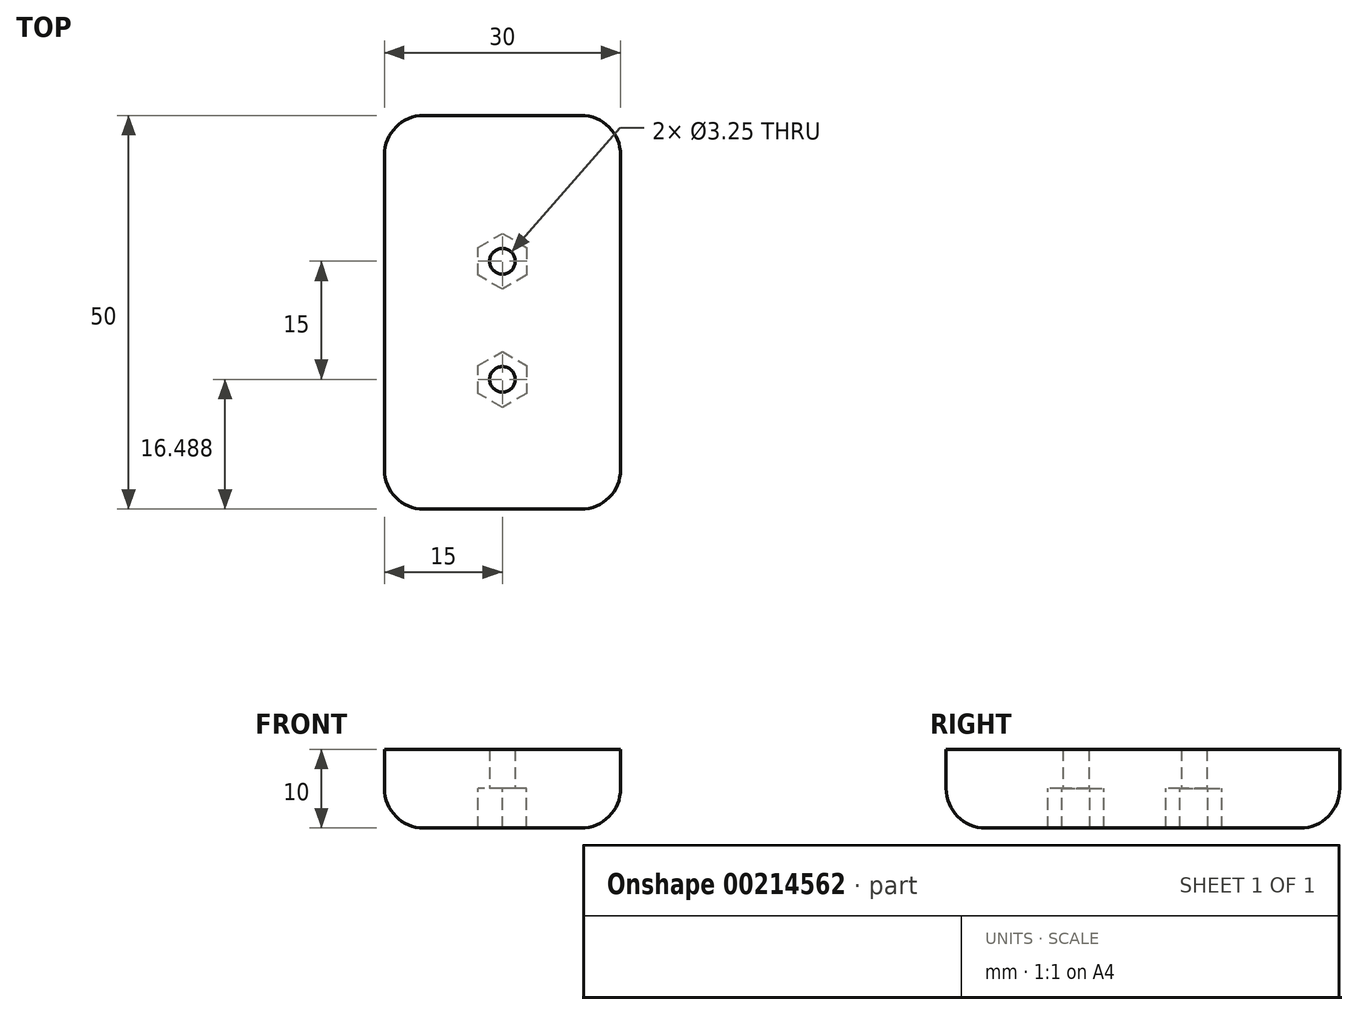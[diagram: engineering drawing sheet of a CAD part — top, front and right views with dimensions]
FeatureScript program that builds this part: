
annotation { "Feature Type Name" : "Feature", "Feature Type Description" : "" }
export const myFeature = defineFeature(function(context is Context, id is Id, definition is map)
    precondition{}
    {
        {
            var Q0;
            Q0=qCreatedBy(makeId("Top.planeOp"),FACE);
            var sketch = newSketch(context, id + "F0", { "sketchPlane" : qUnion([Q0])});
            skCircle(sketch, "E0.cCircle", {"center": v(0, 31.49) * mm, "radius": 3.55 * mm, "construction": true});
            skLineSegment(sketch, "E0.0", {"start": v(0, 27.94) * mm, "end": v(-3.07, 29.71) * mm});
            skLineSegment(sketch, "E0.1", {"start": v(-3.07, 29.71) * mm, "end": v(-3.07, 33.26) * mm});
            skLineSegment(sketch, "E0.2", {"start": v(-3.07, 33.26) * mm, "end": v(0, 35.04) * mm});
            skLineSegment(sketch, "E0.3", {"start": v(0, 35.04) * mm, "end": v(3.07, 33.26) * mm});
            skLineSegment(sketch, "E0.4", {"start": v(3.07, 33.26) * mm, "end": v(3.07, 29.71) * mm});
            skLineSegment(sketch, "E0.5", {"start": v(3.07, 29.71) * mm, "end": v(0, 27.94) * mm});
            skCircle(sketch, "E1.cCircle", {"center": v(0, 16.49) * mm, "radius": 3.55 * mm, "construction": true});
            skLineSegment(sketch, "E1.0", {"start": v(3.07, 14.71) * mm, "end": v(0, 12.94) * mm});
            skLineSegment(sketch, "E1.1", {"start": v(0, 12.94) * mm, "end": v(-3.07, 14.71) * mm});
            skLineSegment(sketch, "E1.2", {"start": v(-3.07, 14.71) * mm, "end": v(-3.07, 18.26) * mm});
            skLineSegment(sketch, "E1.3", {"start": v(-3.07, 18.26) * mm, "end": v(0, 20.04) * mm});
            skLineSegment(sketch, "E1.4", {"start": v(0, 20.04) * mm, "end": v(3.07, 18.26) * mm});
            skLineSegment(sketch, "E1.5", {"start": v(3.07, 18.26) * mm, "end": v(3.07, 14.71) * mm});
            skLineSegment(sketch, "E2.left", {"start": v(-15, 0) * mm, "end": v(-15, 50) * mm});
            skLineSegment(sketch, "E2.right", {"start": v(15, 0) * mm, "end": v(15, 50) * mm});
            skLineSegment(sketch, "E3", {"start": v(15, 50) * mm, "end": v(0, 50) * mm});
            skLineSegment(sketch, "E4", {"start": v(0, 50) * mm, "end": v(-15, 50) * mm});
            skLineSegment(sketch, "E5", {"start": v(-15, 0) * mm, "end": v(0, 0) * mm});
            skLineSegment(sketch, "E6", {"start": v(0, 0) * mm, "end": v(15, 0) * mm});
            skSolve(sketch);
        }
        {
            var Q0;
            Q0=makeQuery(id+"F0.imprint","IMPRINT",FACE,{"disambiguationData":[TD([[makeQuery(id+"F0.imprint","IMPRINT",EDGE,{"derivedFrom":sQuery(id+"F0.wireOp",EDGE,"E0.0")}),1.0]])]});
            extrude(context, id + "F1", {"entities" : qUnion([Q0]), "oppositeDirection" : true, "depth" : 5 * mm});
        }
        {
            var Q0;
            Q0=qCreatedBy(makeId("Top.planeOp"),FACE);
            var sketch = newSketch(context, id + "F2", { "sketchPlane" : qUnion([Q0])});
            skLineSegment(sketch, "E7.bottom", {"start": v(-15, 50) * mm, "end": v(15, 50) * mm});
            skLineSegment(sketch, "E7.top", {"start": v(-15, 0) * mm, "end": v(15, 0) * mm});
            skLineSegment(sketch, "E7.left", {"start": v(-15, 50) * mm, "end": v(-15, 0) * mm});
            skLineSegment(sketch, "E7.right", {"start": v(15, 50) * mm, "end": v(15, 0) * mm});
            skSolve(sketch);
        }
        {
            var Q0;
            Q0 = qSketchRegion(id + "F2", true);
            extrude(context, id + "F3", {"entities" : qUnion([Q0]), "operationType" : NewBodyOperationType.ADD, "depth" : 5 * mm});
        }
        {
            var Q0;
            Q0=makeQuery(id+"F1.opExtrude","CAP_FACE",FACE,{"disambiguationData":[OSD([sQuery(id+"F0.wireOp",EDGE,"E0.0"),sQuery(id+"F0.wireOp",EDGE,"E0.1"),sQuery(id+"F0.wireOp",EDGE,"E0.2"),sQuery(id+"F0.wireOp",EDGE,"E0.3"),sQuery(id+"F0.wireOp",EDGE,"E0.4"),sQuery(id+"F0.wireOp",EDGE,"E0.5"),sQuery(id+"F0.wireOp",EDGE,"E1.0"),sQuery(id+"F0.wireOp",EDGE,"E1.1"),sQuery(id+"F0.wireOp",EDGE,"E1.2"),sQuery(id+"F0.wireOp",EDGE,"E1.3"),sQuery(id+"F0.wireOp",EDGE,"E1.4"),sQuery(id+"F0.wireOp",EDGE,"E1.5"),sQuery(id+"F0.wireOp",EDGE,"E2.left"),sQuery(id+"F0.wireOp",EDGE,"E2.right"),sQuery(id+"F0.wireOp",EDGE,"E3"),sQuery(id+"F0.wireOp",EDGE,"E4"),sQuery(id+"F0.wireOp",EDGE,"E5"),sQuery(id+"F0.wireOp",EDGE,"E6")])],"isStart":false});
            var sketch = newSketch(context, id + "F4", { "sketchPlane" : qUnion([Q0])});
            skCircle(sketch, "E8", {"center": v(0, -16.49) * mm, "radius": 1.62 * mm});
            skPoint(sketch, "E8.centerSnap0", {"position": v(-3.07, -16.49) * mm});
            skPoint(sketch, "E8.perimeterSnap0", {"position": v(-3.07, -16.49) * mm});
            skPoint(sketch, "E8.perimeterSnap1", {"position": v(1.54, -19.15) * mm});
            skCircle(sketch, "E9", {"center": v(0, -31.49) * mm, "radius": 1.62 * mm});
            skPoint(sketch, "E9.centerSnap0", {"position": v(3.07, -31.49) * mm});
            skPoint(sketch, "E9.perimeterSnap0", {"position": v(3.07, -31.49) * mm});
            skSolve(sketch);
        }
        {
            var Q0;
            Q0=makeQuery(id+"F4.imprint","IMPRINT",FACE,{"disambiguationData":[TD([[makeQuery(id+"F4.imprint","IMPRINT",EDGE,{"derivedFrom":sQuery(id+"F4.wireOp",EDGE,"E8")}),1.0]])]});
            var Q1;
            Q1=makeQuery(id+"F4.imprint","IMPRINT",FACE,{"disambiguationData":[TD([[makeQuery(id+"F4.imprint","IMPRINT",EDGE,{"derivedFrom":sQuery(id+"F4.wireOp",EDGE,"E9")}),1.0]])]});
            var Q2;
            Q2=sQuery(id+"F4.wireOp",EDGE,"E9");
            var Q3;
            Q3=sQuery(id+"F4.wireOp",EDGE,"E8");
            extrude(context, id + "F5", {"entities" : qUnion([Q0, Q1]), "operationType" : NewBodyOperationType.REMOVE, "surfaceEntities" : qUnion([Q2, Q3]), "oppositeDirection" : true, "depth" : 25 * mm});
        }
        {
            var Q0;
            Q0=makeQuery(id+"F1.opExtrude","CAP_EDGE",EDGE,{"disambiguationData":[OSD([sQuery(id+"F0.wireOp",EDGE,"E5"),sQuery(id+"F0.wireOp",EDGE,"E6")])],"isStart":false});
            var Q1;
            Q1=makeQuery(id+"F1.opExtrude","CAP_EDGE",EDGE,{"disambiguationData":[OSD([sQuery(id+"F0.wireOp",EDGE,"E2.left")])],"isStart":false});
            var Q2;
            Q2=makeQuery(id+"F1.opExtrude","CAP_EDGE",EDGE,{"disambiguationData":[OSD([sQuery(id+"F0.wireOp",EDGE,"E2.right")])],"isStart":false});
            var Q3;
            Q3=makeQuery(id+"F1.opExtrude","CAP_EDGE",EDGE,{"disambiguationData":[OSD([sQuery(id+"F0.wireOp",EDGE,"E3"),sQuery(id+"F0.wireOp",EDGE,"E4")])],"isStart":false});
            var Q4;
            Q4=makeQuery(id+"F3.boolean.opBoolean","MERGE",EDGE,{"derivedFrom":[makeQuery(id+"F1.opExtrude","SWEPT_EDGE",EDGE,{"disambiguationData":[OSD([sQuery(id+"F0.wireOp",EDGE,"E2.right"),sQuery(id+"F0.wireOp",EDGE,"E3")])]}),makeQuery(id+"F3.opExtrude","SWEPT_EDGE",EDGE,{"disambiguationData":[OSD([sQuery(id+"F2.wireOp",EDGE,"E7.bottom"),sQuery(id+"F2.wireOp",EDGE,"E7.right")])]})]});
            var Q5;
            Q5=makeQuery(id+"F3.boolean.opBoolean","MERGE",EDGE,{"derivedFrom":[makeQuery(id+"F1.opExtrude","SWEPT_EDGE",EDGE,{"disambiguationData":[OSD([sQuery(id+"F0.wireOp",EDGE,"E2.left"),sQuery(id+"F0.wireOp",EDGE,"E5")])]}),makeQuery(id+"F3.opExtrude","SWEPT_EDGE",EDGE,{"disambiguationData":[OSD([sQuery(id+"F2.wireOp",EDGE,"E7.top"),sQuery(id+"F2.wireOp",EDGE,"E7.left")])]})]});
            var Q6;
            Q6=makeQuery(id+"F3.boolean.opBoolean","MERGE",EDGE,{"derivedFrom":[makeQuery(id+"F1.opExtrude","SWEPT_EDGE",EDGE,{"disambiguationData":[OSD([sQuery(id+"F0.wireOp",EDGE,"E2.left"),sQuery(id+"F0.wireOp",EDGE,"E4")])]}),makeQuery(id+"F3.opExtrude","SWEPT_EDGE",EDGE,{"disambiguationData":[OSD([sQuery(id+"F2.wireOp",EDGE,"E7.bottom"),sQuery(id+"F2.wireOp",EDGE,"E7.left")])]})]});
            var Q7;
            Q7=makeQuery(id+"F3.boolean.opBoolean","MERGE",EDGE,{"derivedFrom":[makeQuery(id+"F1.opExtrude","SWEPT_EDGE",EDGE,{"disambiguationData":[OSD([sQuery(id+"F0.wireOp",EDGE,"E2.right"),sQuery(id+"F0.wireOp",EDGE,"E6")])]}),makeQuery(id+"F3.opExtrude","SWEPT_EDGE",EDGE,{"disambiguationData":[OSD([sQuery(id+"F2.wireOp",EDGE,"E7.top"),sQuery(id+"F2.wireOp",EDGE,"E7.right")])]})]});
            fillet(context, id + "F6", {"entities" : qUnion([Q0, Q1, Q2, Q3, Q4, Q5, Q6, Q7]), "radius" : 5 * mm, "tangentPropagation" : true, "allowEdgeOverflow" : false});
        }
    });
